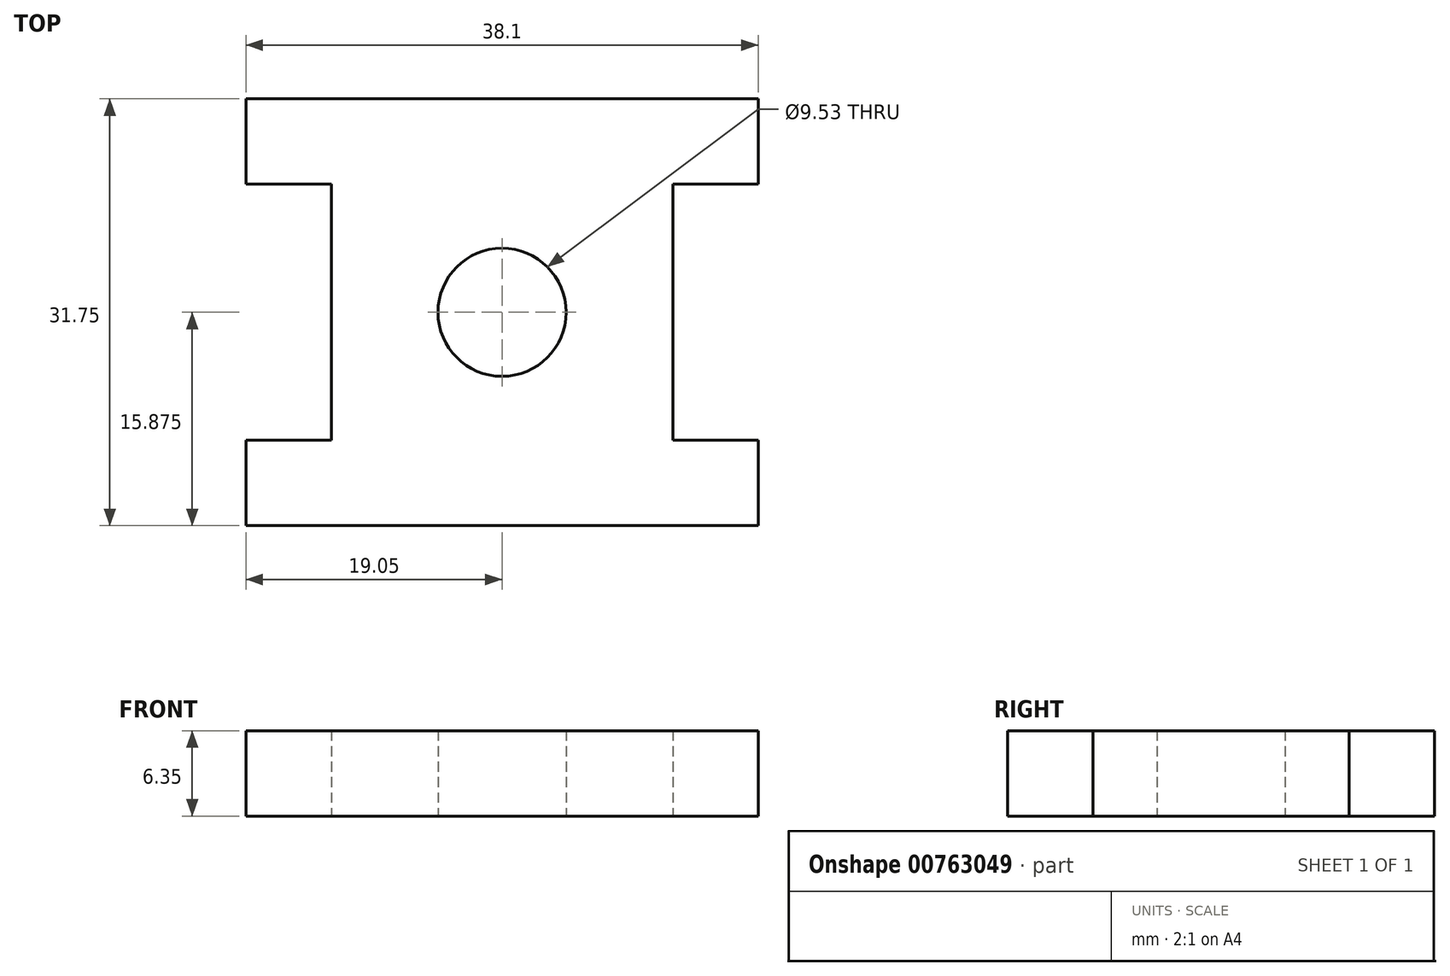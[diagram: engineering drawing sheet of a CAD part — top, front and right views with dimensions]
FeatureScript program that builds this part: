
annotation { "Feature Type Name" : "Feature", "Feature Type Description" : "" }
export const myFeature = defineFeature(function(context is Context, id is Id, definition is map)
    precondition{}
    {
        {
            var Q0;
            Q0=qCreatedBy(makeId("Top.planeOp"),FACE);
            var sketch = newSketch(context, id + "F0", { "sketchPlane" : qUnion([Q0])});
            skLineSegment(sketch, "E0.bottom", {"start": v(0, 0) * mm, "end": v(38.1, 0) * mm});
            skLineSegment(sketch, "E0.top", {"start": v(0, 31.75) * mm, "end": v(38.1, 31.75) * mm});
            skLineSegment(sketch, "E0.left", {"start": v(0, 0) * mm, "end": v(0, 6.35) * mm});
            skLineSegment(sketch, "E0.right", {"start": v(38.1, 0) * mm, "end": v(38.1, 6.35) * mm});
            skLineSegment(sketch, "E1.bottom", {"start": v(0, 6.35) * mm, "end": v(6.35, 6.35) * mm});
            skLineSegment(sketch, "E1.top", {"start": v(0, 25.4) * mm, "end": v(6.35, 25.4) * mm});
            skLineSegment(sketch, "E1.right", {"start": v(6.35, 6.35) * mm, "end": v(6.35, 25.4) * mm});
            skLineSegment(sketch, "E2.bottom", {"start": v(38.1, 6.35) * mm, "end": v(31.75, 6.35) * mm});
            skLineSegment(sketch, "E2.top", {"start": v(38.1, 25.4) * mm, "end": v(31.75, 25.4) * mm});
            skLineSegment(sketch, "E2.right", {"start": v(31.75, 6.35) * mm, "end": v(31.75, 25.4) * mm});
            skLineSegment(sketch, "E3.trimOffspring", {"start": v(0, 25.4) * mm, "end": v(0, 31.75) * mm});
            skLineSegment(sketch, "E4.trimOffspring", {"start": v(38.1, 25.4) * mm, "end": v(38.1, 31.75) * mm});
            skCircle(sketch, "E5", {"center": v(19.05, 15.88) * mm, "radius": 4.76 * mm});
            skSolve(sketch);
        }
        {
            var Q0;
            Q0 = qSketchRegion(id + "F0", true);
            extrude(context, id + "F1", {"entities" : qUnion([Q0]), "depth" : 6.35 * mm, "offsetDistance" : 25.4 * mm});
        }
    });
